FCSTD DOCUMENT  (FreeCAD 0.19R0.19.2)
Label: boatMoterHolder005
License: All rights reserved
LicenseURL: http://en.wikipedia.org/wiki/All_rights_reserved
objects: Sketcher::SketchObject×1
note: 1 computed .brp shape members not serialized (recipe doc carries the construction recipe); baked Part::Feature solids carry a one-line shape summary decoded from their .brp

FEATURE [Sketcher::SketchObject] Sketch
  FullyConstrained = false
  sketch-geometry (48):
    g0: Circle CenterX=-6 CenterY=0 CenterZ=0 NormalX=0 NormalY=0 NormalZ=1 AngleXU=0 Radius=0.9
    g1: Circle CenterX=0 CenterY=6 CenterZ=0 NormalX=0 NormalY=0 NormalZ=1 AngleXU=0 Radius=0.9
    g2: Circle CenterX=6 CenterY=0 CenterZ=0 NormalX=0 NormalY=0 NormalZ=1 AngleXU=0 Radius=0.9
    g3: Circle CenterX=0 CenterY=-6 CenterZ=0 NormalX=0 NormalY=0 NormalZ=1 AngleXU=0 Radius=0.9
    g4: LineSegment StartX=3.53553 StartY=-3.53553 StartZ=0 EndX=4.94975 EndY=-4.94975 EndZ=0
    g5: LineSegment StartX=3.53553 StartY=3.53553 StartZ=0 EndX=4.94975 EndY=4.94975 EndZ=0
    g6: LineSegment StartX=4.94975 StartY=-4.94975 StartZ=0 EndX=6.34846 EndY=-3.5202 EndZ=0
    g7: LineSegment StartX=4.94975 StartY=-4.94975 StartZ=0 EndX=3.53551 EndY=-6.36394 EndZ=0
    g8-g12: Circle x5 (B-spline internal-alignment scaffolding for g13; pole/knot coordinates omitted)
    g13: BSplineCurve PolesCount=5 KnotsCount=3 Degree=3 IsPeriodic=0
    g14: GeomPoint X=-4.94974 Y=10.6066 Z=0
    g15: GeomPoint X=-4.24264 Y=4.24264 Z=0
    g16: GeomPoint X=-10.6066 Y=4.94975 Z=0
    g17-g21: Circle x5 (B-spline internal-alignment scaffolding for g22; pole/knot coordinates omitted)
    g22: BSplineCurve PolesCount=5 KnotsCount=3 Degree=3 IsPeriodic=0
    g23: GeomPoint X=-10.6066 Y=-4.94974 Z=0
    g24: GeomPoint X=-4.23566 Y=-4.23553 Z=0
    g25: GeomPoint X=-4.94053 Y=-10.6109 Z=0
    g26-g30: Circle x5 (B-spline internal-alignment scaffolding for g31; pole/knot coordinates omitted)
    g31: BSplineCurve PolesCount=5 KnotsCount=3 Degree=3 IsPeriodic=0
    g32: GeomPoint X=4.94975 Y=-10.6066 Z=0
    g33: GeomPoint X=4.23876 Y=-4.2388 Z=0
    g34: GeomPoint X=10.603 Y=-4.95737 Z=0
    g35-g39: Circle x5 (B-spline internal-alignment scaffolding for g40; pole/knot coordinates omitted)
    g40: BSplineCurve PolesCount=5 KnotsCount=3 Degree=3 IsPeriodic=0
    g41: GeomPoint X=10.6066 Y=4.94975 Z=0
    g42: GeomPoint X=4.24264 Y=4.24264 Z=0
    g43: GeomPoint X=4.94975 Y=10.6066 Z=0
    g44: ArcOfCircle CenterX=0 CenterY=0 CenterZ=0 NormalX=0 NormalY=0 NormalZ=1 AngleXU=0 Radius=11.7047 StartAngle=1.13417 EndAngle=2.00742
    g45: ArcOfCircle CenterX=0 CenterY=0 CenterZ=0 NormalX=0 NormalY=0 NormalZ=1 AngleXU=0 Radius=11.7047 StartAngle=5.84584 EndAngle=6.71981
    g46: ArcOfCircle CenterX=0 CenterY=0 CenterZ=0 NormalX=0 NormalY=0 NormalZ=1 AngleXU=0 Radius=11.7047 StartAngle=4.27663 EndAngle=5.14902
    g47: ArcOfCircle CenterX=0 CenterY=0 CenterZ=0 NormalX=0 NormalY=0 NormalZ=1 AngleXU=0 Radius=11.7047 StartAngle=2.70497 EndAngle=3.57822
  constraints (49):
    c: Block(g1)
    c: Block(g2)
    c: Block(g3)
    c: Block(g0)
    c: Distance(g4) = 2
    c: Distance(g5) = 2
    c: Coincident(g6,g4)
    c: Coincident(g7,g4)
    c: Weight(g8) = 1
    c: Equal(g8, g9-g12) x4
    c: InternalAlignment(g8-g12 -> g13) x5
    c: InternalAlignment(g14,g13)
    c: InternalAlignment(g15,g13)
    c: InternalAlignment(g16,g13)
    c: Weight(g17) = 1
    c: Equal(g17, g18-g21) x4
    c: InternalAlignment(g17-g21 -> g22) x5
    c: InternalAlignment(g23,g22)
    c: InternalAlignment(g24,g22)
    c: InternalAlignment(g25,g22)
    c: Weight(g26) = 1
    c: Equal(g26,g27)
    c: Coincident(g27,g7)
    c: Equal(g26,g28)
    c: Equal(g26,g29)
    c: Coincident(g29,g6)
    c: Equal(g26,g30)
    c: InternalAlignment(g26-g30 -> g31) x5
    c: InternalAlignment(g32,g31)
    c: InternalAlignment(g33,g31)
    c: InternalAlignment(g34,g31)
    c: Weight(g35) = 1
    c: Equal(g35, g36-g39) x4
    c: InternalAlignment(g35-g39 -> g40) x5
    c: InternalAlignment(g41,g40)
    c: InternalAlignment(g42,g40)
    c: InternalAlignment(g43,g40)
    c: Coincident(g44,g-1)
    c: Coincident(g44,g13)
    c: Coincident(g44,g40)
    c: Coincident(g45,g44)
    c: Coincident(g45,g40)
    c: Coincident(g45,g31)
    c: Coincident(g46,g44)
    c: Coincident(g46,g31)
    c: Coincident(g46,g22)
    c: Coincident(g47,g44)
    c: Coincident(g47,g22)
    c: Coincident(g47,g13)
